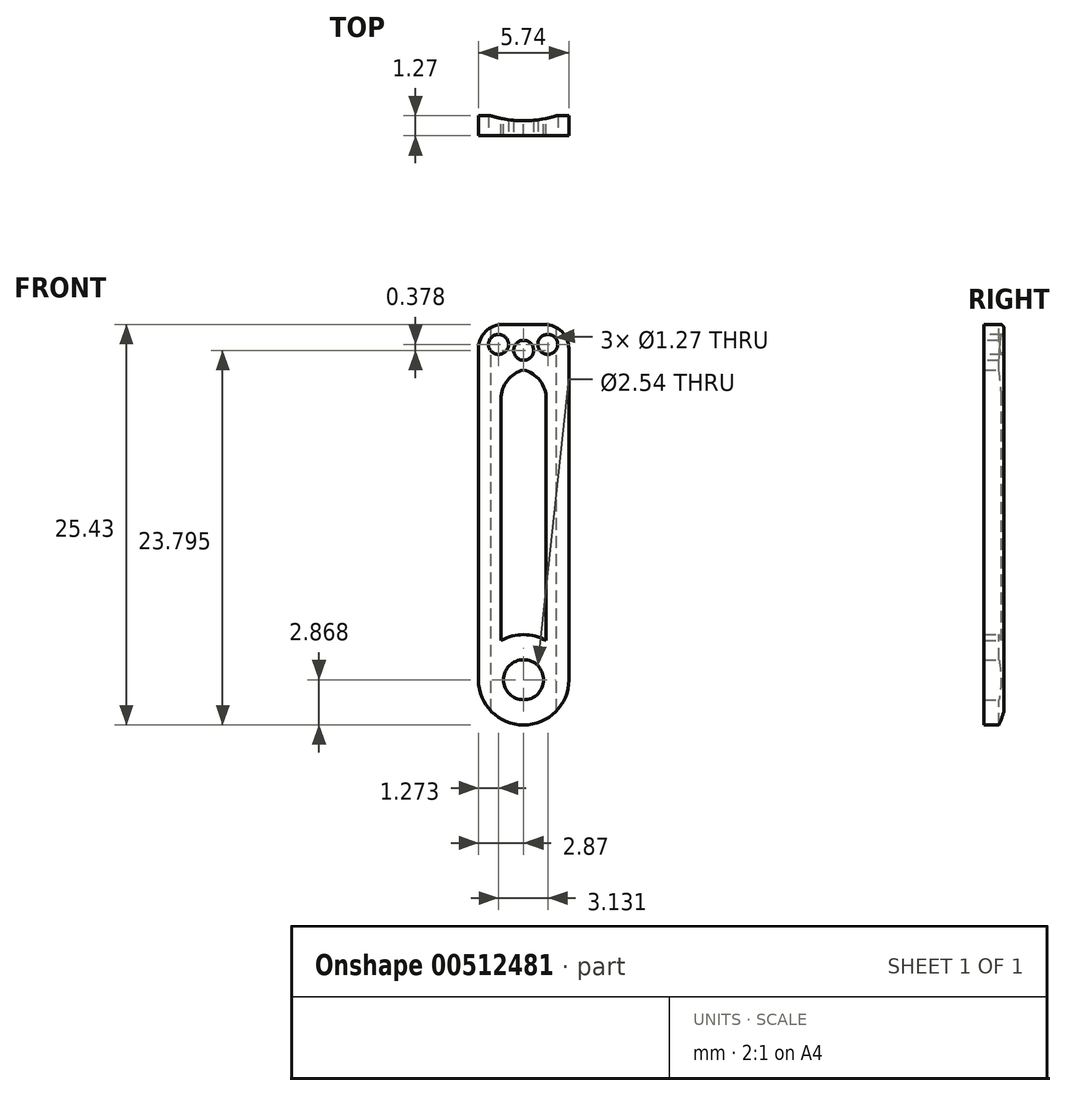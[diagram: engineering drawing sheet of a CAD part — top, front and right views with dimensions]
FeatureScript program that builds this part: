
annotation { "Feature Type Name" : "Feature", "Feature Type Description" : "" }
export const myFeature = defineFeature(function(context is Context, id is Id, definition is map)
    precondition{}
    {
        {
            var Q0;
            Q0=qCreatedBy(makeId("Front.planeOp"),FACE);
            var sketch = newSketch(context, id + "F0", { "sketchPlane" : qUnion([Q0])});
            skCircle(sketch, "E0", {"center": v(0, 2.87) * mm, "radius": 2.87 * mm});
            skLineSegment(sketch, "E1", {"start": v(0, 25.43) * mm, "end": v(2.87, 25.43) * mm});
            skLineSegment(sketch, "E2", {"start": v(2.87, 25.43) * mm, "end": v(2.87, 2.87) * mm});
            skLineSegment(sketch, "E3", {"start": v(-2.87, 2.87) * mm, "end": v(-2.87, 25.43) * mm});
            skLineSegment(sketch, "E4", {"start": v(-2.87, 25.43) * mm, "end": v(2.87, 25.43) * mm});
            skLineSegment(sketch, "E5", {"start": v(-2.87, 25.43) * mm, "end": v(0, 25.43) * mm});
            skLineSegment(sketch, "E6", {"start": v(-2.87, 25.43) * mm, "end": v(-1.43, 25.43) * mm});
            skLineSegment(sketch, "E7", {"start": v(1.43, 5.35) * mm, "end": v(1.43, 22.6) * mm});
            skLineSegment(sketch, "E8", {"start": v(-1.43, 5.35) * mm, "end": v(-1.43, 22.6) * mm});
            skLineSegment(sketch, "E9", {"start": v(-1.43, 22.6) * mm, "end": v(1.43, 22.6) * mm});
            skSolve(sketch);
        }
        {
            var Q0;
            {var subQ0=sQuery(id+"F0.wireOp",EDGE,"E2");Q0=makeQuery(id+"F0.imprint","IMPRINT",FACE,{"disambiguationData":[TD([[makeQuery(id+"F0.imprint","IMPRINT",EDGE,{"derivedFrom":subQ0}),-1.0]])]});}
            var Q1;
            {var subQ0=sQuery(id+"F0.wireOp",EDGE,"E0");var subQ1=makeQuery(id+"F0.imprint","INTERSECT",VERTEX,{"derivedFrom":[subQ0,sQuery(id+"F0.wireOp",EDGE,"E2")]});Q1=makeQuery(id+"F0.imprint","IMPRINT",FACE,{"disambiguationData":[TD([[makeQuery(id+"F0.imprint","IMPRINT",EDGE,{"disambiguationData":[TD([[subQ1,-1.0]])],"derivedFrom":subQ0}),1.0]])]});}
            extrude(context, id + "F1", {"entities" : qUnion([Q0, Q1]), "depth" : 1.27 * mm});
        }
        {
            var Q0;
            Q0=makeQuery(id+"F1.opExtrude","CAP_FACE",FACE,{"disambiguationData":[OSD([sQuery(id+"F0.wireOp",EDGE,"E0"),sQuery(id+"F0.wireOp",EDGE,"E2"),sQuery(id+"F0.wireOp",EDGE,"E3"),sQuery(id+"F0.wireOp",EDGE,"E4"),sQuery(id+"F0.wireOp",EDGE,"E5"),sQuery(id+"F0.wireOp",EDGE,"E6"),sQuery(id+"F0.wireOp",EDGE,"E7"),sQuery(id+"F0.wireOp",EDGE,"E8"),sQuery(id+"F0.wireOp",EDGE,"E9")])],"isStart":true});
            var sketch = newSketch(context, id + "F2", { "sketchPlane" : qUnion([Q0])});
            skCircle(sketch, "E10", {"center": v(0, 2.87) * mm, "radius": 1.43 * mm});
            skCircle(sketch, "E11", {"center": v(0, 2.87) * mm, "radius": 1.98 * mm});
            skSolve(sketch);
        }
        {
            var Q0;
            Q0=sQuery(id+"F2.wireOp",VERTEX,"E10.center");
            var Q1;
            Q1=makeQuery(id+"F1.opExtrude","SWEPT_BODY",BODY,{"disambiguationData":[OSD([sQuery(id+"F0.wireOp",EDGE,"E0"),sQuery(id+"F0.wireOp",EDGE,"E2"),sQuery(id+"F0.wireOp",EDGE,"E3"),sQuery(id+"F0.wireOp",EDGE,"E4"),sQuery(id+"F0.wireOp",EDGE,"E5"),sQuery(id+"F0.wireOp",EDGE,"E6"),sQuery(id+"F0.wireOp",EDGE,"E7"),sQuery(id+"F0.wireOp",EDGE,"E8"),sQuery(id+"F0.wireOp",EDGE,"E9")])]});
            hole(context, id + "F3", {"style" : HoleStyle.SIMPLE, "endStyle" : HoleEndStyle.BLIND, "holeDiameter" : 2.54 * mm, "holeDepth" : 6.35 * mm, "isTappedThrough" : true, "tappedDepth" : 12.7 * mm, "tapClearance" : 3, "locations" : qUnion([Q0]), "scope" : qUnion([Q1])});
        }
        {
            var Q0;
            Q0=makeQuery(id+"F1.opExtrude","SWEPT_EDGE",EDGE,{"disambiguationData":[OSD([sQuery(id+"F0.wireOp",EDGE,"E2"),sQuery(id+"F0.wireOp",EDGE,"E4")])]});
            var Q1;
            Q1=makeQuery(id+"F1.opExtrude","SWEPT_EDGE",EDGE,{"disambiguationData":[OSD([sQuery(id+"F0.wireOp",EDGE,"E3"),sQuery(id+"F0.wireOp",EDGE,"E6")])]});
            fillet(context, id + "F4", {"entities" : qUnion([Q0, Q1]), "radius" : 1.52 * mm, "tangentPropagation" : true, "allowEdgeOverflow" : false});
        }
        {
            var Q0;
            Q0=makeQuery(id+"F1.opExtrude","CAP_FACE",FACE,{"disambiguationData":[OSD([sQuery(id+"F0.wireOp",EDGE,"E0"),sQuery(id+"F0.wireOp",EDGE,"E2"),sQuery(id+"F0.wireOp",EDGE,"E3"),sQuery(id+"F0.wireOp",EDGE,"E4"),sQuery(id+"F0.wireOp",EDGE,"E5"),sQuery(id+"F0.wireOp",EDGE,"E6"),sQuery(id+"F0.wireOp",EDGE,"E7"),sQuery(id+"F0.wireOp",EDGE,"E8"),sQuery(id+"F0.wireOp",EDGE,"E9")])],"isStart":false});
            var sketch = newSketch(context, id + "F5", { "sketchPlane" : qUnion([Q0])});
            skLineSegment(sketch, "E12", {"start": v(-2.42, 24.98) * mm, "end": v(0, 22.6) * mm});
            skLineSegment(sketch, "E13", {"start": v(0, 22.6) * mm, "end": v(2.37, 25.03) * mm});
            skPoint(sketch, "E14.startSnap0", {"position": v(-1.21, 23.8) * mm});
            skLineSegment(sketch, "E15", {"start": v(-1.21, 23.8) * mm, "end": v(1.16, 23.8) * mm});
            skLineSegment(sketch, "E16", {"start": v(-2.87, 23.9) * mm, "end": v(2.87, 23.9) * mm});
            skLineSegment(sketch, "E17", {"start": v(0, 23.9) * mm, "end": v(0, 23.8) * mm});
            skLineSegment(sketch, "E18", {"start": v(0, 23.8) * mm, "end": v(1.16, 23.8) * mm});
            skLineSegment(sketch, "E19", {"start": v(0, 23.8) * mm, "end": v(0.58, 23.8) * mm});
            skCircle(sketch, "E20", {"center": v(0, 23.85) * mm, "radius": 0.58 * mm});
            skLineSegment(sketch, "E21", {"start": v(-2.42, 24.98) * mm, "end": v(-1.32, 23.9) * mm});
            skLineSegment(sketch, "E22", {"start": v(-1.32, 23.9) * mm, "end": v(-1.87, 24.44) * mm});
            skLineSegment(sketch, "E23", {"start": v(-1.87, 24.44) * mm, "end": v(1.8, 24.44) * mm});
            skLineSegment(sketch, "E24", {"start": v(1.8, 24.44) * mm, "end": v(1.27, 23.9) * mm});
            skLineSegment(sketch, "E25", {"start": v(1.8, 24.44) * mm, "end": v(1.53, 24.17) * mm});
            skLineSegment(sketch, "E26", {"start": v(1.53, 24.17) * mm, "end": v(-1.6, 24.17) * mm});
            skCircle(sketch, "E27", {"center": v(-1.6, 24.17) * mm, "radius": 0.38 * mm});
            skCircle(sketch, "E28", {"center": v(1.53, 24.17) * mm, "radius": 0.38 * mm});
            skSolve(sketch);
        }
        {
            var Q0;
            Q0=sQuery(id+"F5.wireOp",VERTEX,"E27.center");
            var Q1;
            Q1=sQuery(id+"F5.wireOp",VERTEX,"E19.start");
            var Q2;
            Q2=sQuery(id+"F5.wireOp",VERTEX,"E28.center");
            var Q3;
            Q3=makeQuery(id+"F1.opExtrude","SWEPT_BODY",BODY,{"disambiguationData":[OSD([sQuery(id+"F0.wireOp",EDGE,"E0"),sQuery(id+"F0.wireOp",EDGE,"E2"),sQuery(id+"F0.wireOp",EDGE,"E3"),sQuery(id+"F0.wireOp",EDGE,"E4"),sQuery(id+"F0.wireOp",EDGE,"E5"),sQuery(id+"F0.wireOp",EDGE,"E6"),sQuery(id+"F0.wireOp",EDGE,"E7"),sQuery(id+"F0.wireOp",EDGE,"E8"),sQuery(id+"F0.wireOp",EDGE,"E9")])]});
            hole(context, id + "F6", {"style" : HoleStyle.SIMPLE, "endStyle" : HoleEndStyle.BLIND, "holeDiameter" : 1.27 * mm, "holeDepth" : 6.35 * mm, "isTappedThrough" : true, "tappedDepth" : 12.7 * mm, "tapClearance" : 3, "locations" : qUnion([Q0, Q1, Q2]), "scope" : qUnion([Q3])});
        }
        {
            var Q0;
            Q0=makeQuery(id+"F1.opExtrude","SWEPT_EDGE",EDGE,{"disambiguationData":[OSD([sQuery(id+"F0.wireOp",EDGE,"E7"),sQuery(id+"F0.wireOp",EDGE,"E9")])]});
            var Q1;
            Q1=makeQuery(id+"F1.opExtrude","SWEPT_EDGE",EDGE,{"disambiguationData":[OSD([sQuery(id+"F0.wireOp",EDGE,"E8"),sQuery(id+"F0.wireOp",EDGE,"E9")])]});
            fillet(context, id + "F7", {"entities" : qUnion([Q0, Q1]), "radius" : 1.9 * mm, "tangentPropagation" : true, "allowEdgeOverflow" : false});
        }
        {
            var Q0;
            Q0=makeQuery(id+"F1.opExtrude","SWEPT_FACE",FACE,{"disambiguationData":[OSD([sQuery(id+"F0.wireOp",EDGE,"E4"),sQuery(id+"F0.wireOp",EDGE,"E5"),sQuery(id+"F0.wireOp",EDGE,"E6")])]});
            var sketch = newSketch(context, id + "F8", { "sketchPlane" : qUnion([Q0])});
            skLineSegment(sketch, "E29", {"start": v(0, 0) * mm, "end": v(0, -1.27) * mm});
            skLineSegment(sketch, "E30", {"start": v(0, 0) * mm, "end": v(0, -0.64) * mm});
            skLineSegment(sketch, "E31", {"start": v(0, -0.64) * mm, "end": v(0, 6.6) * mm});
            skPoint(sketch, "E31.endSnap0", {"position": v(0, -0.32) * mm});
            skCircle(sketch, "E32", {"center": v(0, 6.6) * mm, "radius": 6.92 * mm});
            skSolve(sketch);
        }
        {
            var Q0;
            Q0=sQuery(id+"F8.wireOp",VERTEX,"E32.center");
            var Q1;
            Q1=makeQuery(id+"F1.opExtrude","SWEPT_BODY",BODY,{"disambiguationData":[OSD([sQuery(id+"F0.wireOp",EDGE,"E0"),sQuery(id+"F0.wireOp",EDGE,"E2"),sQuery(id+"F0.wireOp",EDGE,"E3"),sQuery(id+"F0.wireOp",EDGE,"E4"),sQuery(id+"F0.wireOp",EDGE,"E5"),sQuery(id+"F0.wireOp",EDGE,"E6"),sQuery(id+"F0.wireOp",EDGE,"E7"),sQuery(id+"F0.wireOp",EDGE,"E8"),sQuery(id+"F0.wireOp",EDGE,"E9")])]});
            hole(context, id + "F9", {"style" : HoleStyle.SIMPLE, "endStyle" : HoleEndStyle.BLIND, "holeDiameter" : 13.84 * mm, "holeDepth" : 304.8 * mm, "isTappedThrough" : true, "tappedDepth" : 12.7 * mm, "tapClearance" : 3, "locations" : qUnion([Q0]), "scope" : qUnion([Q1])});
        }
    });
